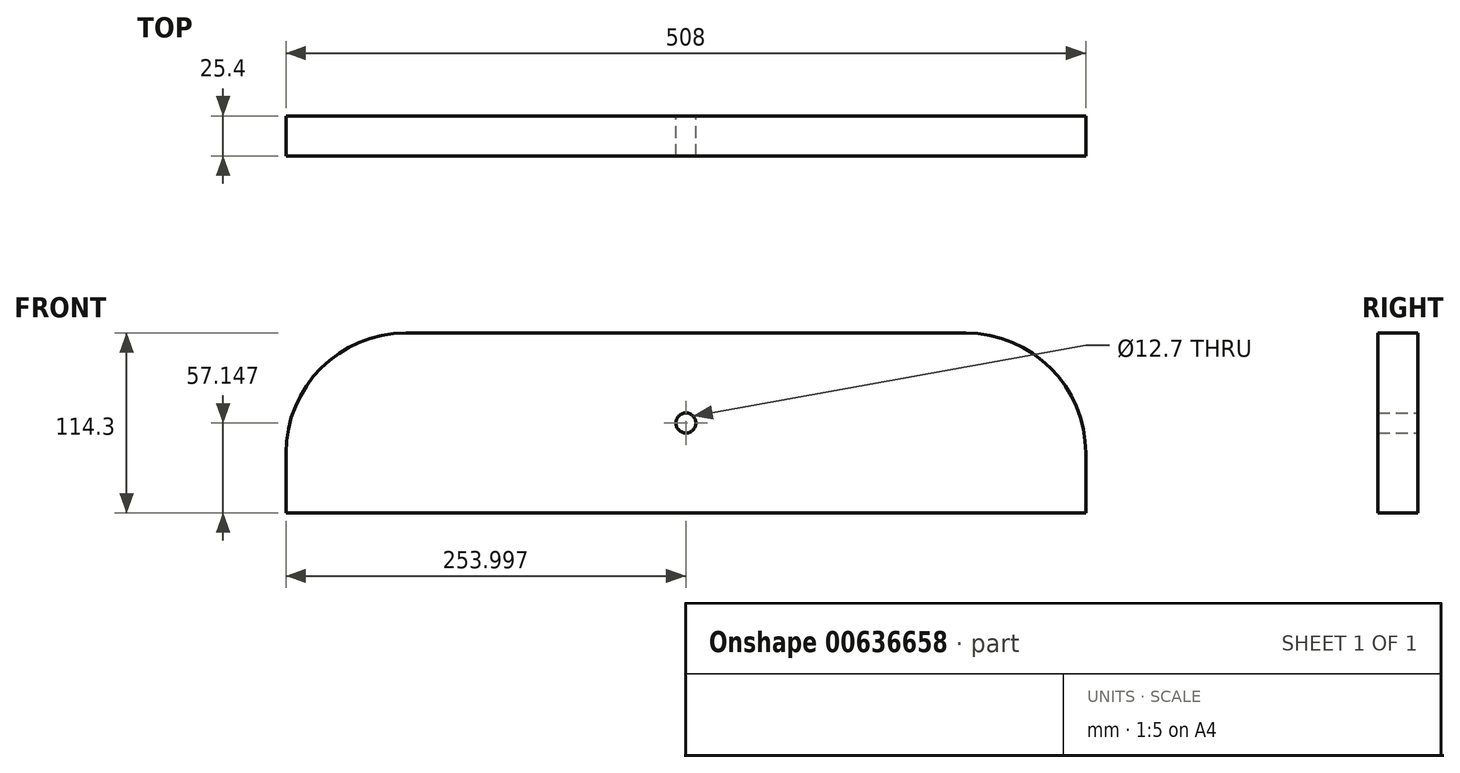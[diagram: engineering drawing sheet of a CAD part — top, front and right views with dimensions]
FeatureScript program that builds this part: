
annotation { "Feature Type Name" : "Feature", "Feature Type Description" : "" }
export const myFeature = defineFeature(function(context is Context, id is Id, definition is map)
    precondition{}
    {
        {
            var Q0;
            Q0=qCreatedBy(makeId("Front.planeOp"),FACE);
            var sketch = newSketch(context, id + "F0", { "sketchPlane" : qUnion([Q0])});
            skLineSegment(sketch, "E0.bottom", {"start": v(-107.64, 31.1) * mm, "end": v(120.96, 31.1) * mm});
            skLineSegment(sketch, "E0.top", {"start": v(-247.34, -83.2) * mm, "end": v(260.66, -83.2) * mm});
            skLineSegment(sketch, "E1", {"start": v(-107.64, 31.1) * mm, "end": v(-107.64, -83.2) * mm, "construction": true});
            skLineSegment(sketch, "E2", {"start": v(120.96, 31.1) * mm, "end": v(120.96, -83.2) * mm, "construction": true});
            skLineSegment(sketch, "E3", {"start": v(-247.34, -83.2) * mm, "end": v(-247.34, -45.1) * mm});
            skLineSegment(sketch, "E4", {"start": v(-171.14, 31.1) * mm, "end": v(-107.64, 31.1) * mm});
            skLineSegment(sketch, "E5", {"start": v(120.96, 31.1) * mm, "end": v(184.46, 31.1) * mm});
            skLineSegment(sketch, "E6", {"start": v(260.66, -45.1) * mm, "end": v(260.66, -83.2) * mm});
            skPoint(sketch, "E7.visualSharp", {"position": v(-247.34, 31.1) * mm});
            skArc(sketch, "E7.filletArc", {"start": v(-171.14, 31.1) * mm, "mid": v(-225.02, 8.79) * mm, "end": v(-247.34, -45.1) * mm});
            skPoint(sketch, "E8.visualSharp", {"position": v(260.66, 31.1) * mm});
            skArc(sketch, "E8.filletArc", {"start": v(260.66, -45.1) * mm, "mid": v(238.34, 8.79) * mm, "end": v(184.46, 31.1) * mm});
            skLineSegment(sketch, "E9", {"start": v(6.66, 31.1) * mm, "end": v(6.66, -83.2) * mm, "construction": true});
            skCircle(sketch, "E10", {"center": v(6.66, -26.04) * mm, "radius": 6.35 * mm});
            skPoint(sketch, "E10.perimeterSnap0", {"position": v(6.66, -26.04) * mm});
            skLineSegment(sketch, "E11", {"start": v(-221.94, 11.7) * mm, "end": v(-221.94, -83.2) * mm, "construction": true});
            skLineSegment(sketch, "E12", {"start": v(235.26, 11.7) * mm, "end": v(235.26, -83.2) * mm, "construction": true});
            skSolve(sketch);
        }
        {
            var Q0;
            Q0 = qSketchRegion(id + "F0", true);
            extrude(context, id + "F1", {"entities" : qUnion([Q0]), "depth" : 25.4 * mm, "offsetDistance" : 25.4 * mm});
        }
    });
